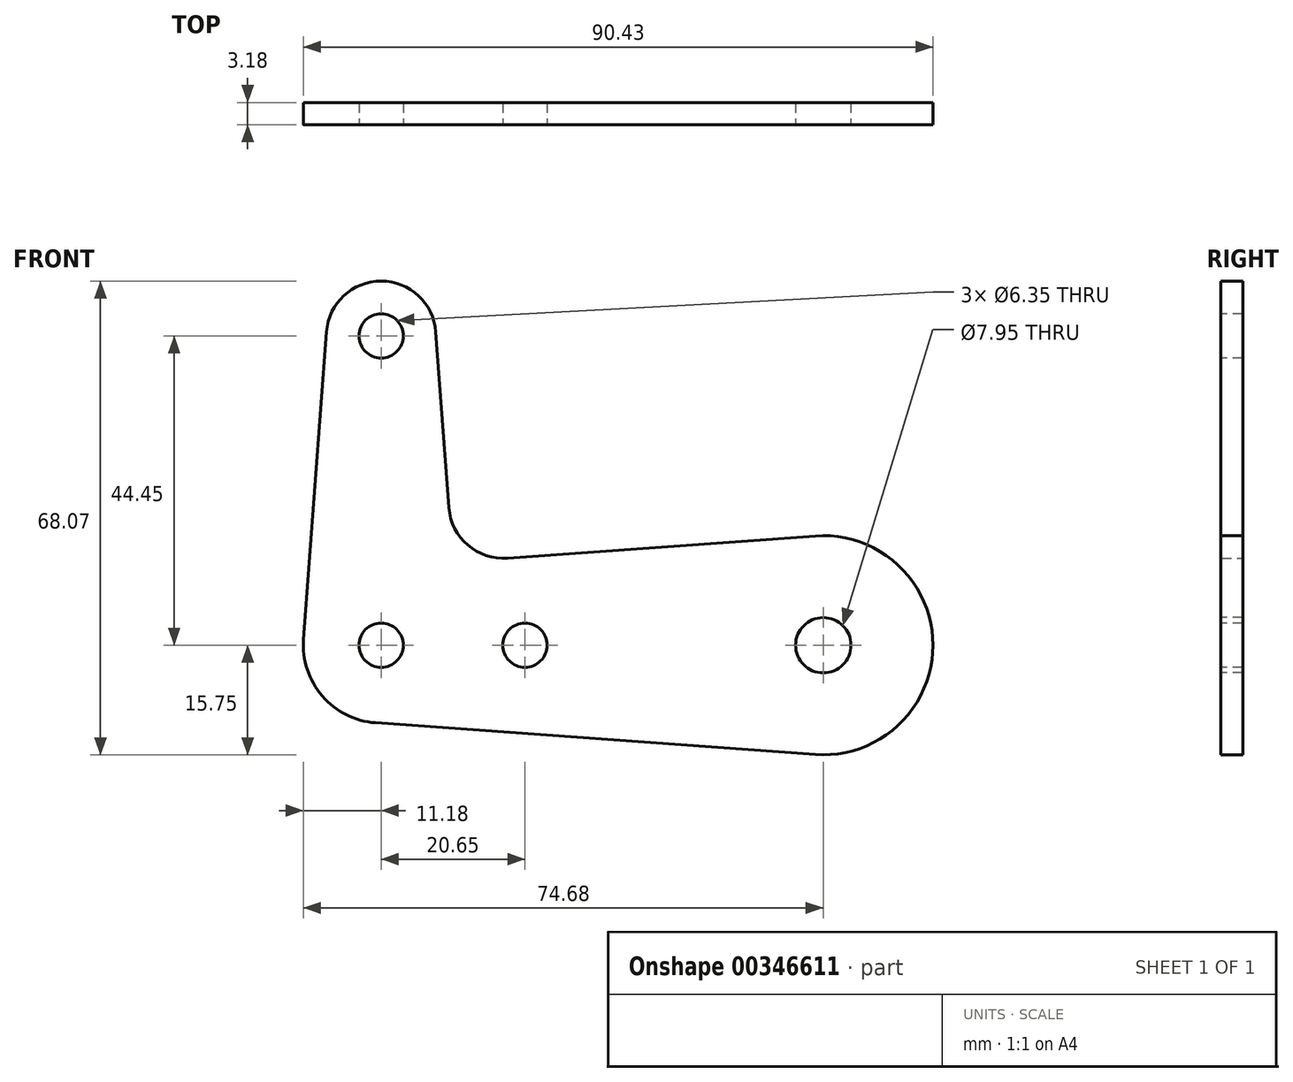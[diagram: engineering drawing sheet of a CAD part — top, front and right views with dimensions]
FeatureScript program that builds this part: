
annotation { "Feature Type Name" : "Feature", "Feature Type Description" : "" }
export const myFeature = defineFeature(function(context is Context, id is Id, definition is map)
    precondition{}
    {
        {
            var Q0;
            Q0=qCreatedBy(makeId("Front.planeOp"),FACE);
            var sketch = newSketch(context, id + "F0", { "sketchPlane" : qUnion([Q0])});
            skCircle(sketch, "E0", {"center": v(0, 0) * mm, "radius": 15.75 * mm});
            skCircle(sketch, "E1", {"center": v(-63.5, 0) * mm, "radius": 11.18 * mm});
            skCircle(sketch, "E2", {"center": v(-63.5, 44.45) * mm, "radius": 7.87 * mm});
            skLineSegment(sketch, "E3", {"start": v(-64.3, -11.15) * mm, "end": v(-1.13, -15.7) * mm});
            skLineSegment(sketch, "E4", {"start": v(-71.35, 45.03) * mm, "end": v(-74.65, 0.83) * mm});
            skLineSegment(sketch, "E5", {"start": v(-55.65, 45.03) * mm, "end": v(-53.77, 19.78) * mm});
            skLineSegment(sketch, "E6", {"start": v(-1.13, 15.7) * mm, "end": v(-45.35, 12.52) * mm});
            skArc(sketch, "E7", {"start": v(-53.77, 19.78) * mm, "mid": v(-51.06, 14.4) * mm, "end": v(-45.35, 12.52) * mm});
            skLineSegment(sketch, "E8", {"start": v(-63.5, 44.45) * mm, "end": v(-63.5, 22.83) * mm});
            skLineSegment(sketch, "E9", {"start": v(0, 0) * mm, "end": v(-25.52, 0) * mm});
            skSolve(sketch);
        }
        {
            var Q0;
            {var subQ0=sQuery(id+"F0.wireOp",EDGE,"E3");Q0=makeQuery(id+"F0.imprint","IMPRINT",FACE,{"disambiguationData":[TD([[makeQuery(id+"F0.imprint","IMPRINT",EDGE,{"derivedFrom":subQ0}),1.0]])]});}
            var Q1;
            {var subQ0=sQuery(id+"F0.wireOp",EDGE,"E1");var subQ1=makeQuery(id+"F0.imprint","INTERSECT",VERTEX,{"derivedFrom":[subQ0,sQuery(id+"F0.wireOp",EDGE,"E3")]});Q1=makeQuery(id+"F0.imprint","IMPRINT",FACE,{"disambiguationData":[TD([[makeQuery(id+"F0.imprint","IMPRINT",EDGE,{"disambiguationData":[TD([[subQ1,1.0]])],"derivedFrom":subQ0}),1.0]])]});}
            var Q2;
            {var subQ0=sQuery(id+"F0.wireOp",EDGE,"E2");var subQ3=makeQuery(id+"F0.imprint","IMPRINT",VERTEX,{"derivedFrom":subQ0});Q2=makeQuery(id+"F0.imprint","IMPRINT",FACE,{"disambiguationData":[TD([[makeQuery(id+"F0.imprint","IMPRINT",EDGE,{"disambiguationData":[TD([[subQ3,1.0]])],"derivedFrom":subQ0}),1.0]])]});}
            var Q3;
            {var subQ0=sQuery(id+"F0.wireOp",EDGE,"E0");var subQ2=makeQuery(id+"F0.imprint","IMPRINT",VERTEX,{"derivedFrom":subQ0});Q3=makeQuery(id+"F0.imprint","IMPRINT",FACE,{"disambiguationData":[TD([[makeQuery(id+"F0.imprint","IMPRINT",EDGE,{"disambiguationData":[TD([[subQ2,1.0]])],"derivedFrom":subQ0}),1.0]])]});}
            extrude(context, id + "F1", {"entities" : qUnion([Q0, Q1, Q2, Q3]), "depth" : 3.17 * mm});
        }
        {
            var Q0;
            Q0=makeQuery(id+"F1.opExtrude","CAP_FACE",FACE,{"disambiguationData":[OSD([sQuery(id+"F0.wireOp",EDGE,"E0"),sQuery(id+"F0.wireOp",EDGE,"E1"),sQuery(id+"F0.wireOp",EDGE,"E2"),sQuery(id+"F0.wireOp",EDGE,"E3"),sQuery(id+"F0.wireOp",EDGE,"E4"),sQuery(id+"F0.wireOp",EDGE,"E5"),sQuery(id+"F0.wireOp",EDGE,"E6"),sQuery(id+"F0.wireOp",EDGE,"E7")])],"isStart":false});
            var sketch = newSketch(context, id + "F2", { "sketchPlane" : qUnion([Q0])});
            skCircle(sketch, "E10", {"center": v(0, 0) * mm, "radius": 3.98 * mm});
            skCircle(sketch, "E11", {"center": v(-63.5, 0) * mm, "radius": 3.18 * mm});
            skCircle(sketch, "E12", {"center": v(-42.85, 0) * mm, "radius": 3.18 * mm});
            skCircle(sketch, "E13", {"center": v(-63.5, 44.45) * mm, "radius": 3.18 * mm});
            skSolve(sketch);
        }
        {
            var Q0;
            Q0 = qSketchRegion(id + "F2", true);
            extrude(context, id + "F3", {"entities" : qUnion([Q0]), "operationType" : NewBodyOperationType.REMOVE, "endBound" : BoundingType.THROUGH_ALL, "oppositeDirection" : true, "depth" : 25.4 * mm});
        }
    });
